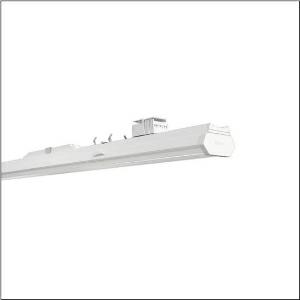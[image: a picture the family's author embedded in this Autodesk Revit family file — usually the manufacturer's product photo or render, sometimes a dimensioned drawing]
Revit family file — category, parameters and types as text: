
# Revit family: licross_r__21_protected_mo_52td1bdn4axg_daa2
name_source: partatom
category: Lighting Fixtures
units: mm (PartAtom-declared; Revit-internal decimal feet)

## family parameters
Cut with Voids When Loaded = No
Host = Face
Light Source = No
Part Type = Normal
Room Calculation Point = No
Round Connector Dimension = Use Diameter
Shared = No

## types (1)
- --- (1 x LED, 10050 lm, 62 W, 4000K)
    Apparent Load = 62 VA
    CIE Flux Codes = 54 82 95 97 100
    Color Rendering = 80
    Color Temperature = 4000K
    Default Elevation = 1800 mm
    Description = Licross® 21 Protected MO, luminaire insert, of sheet steel, galvanised, coil coated, white, length: 1.500mm, width: 90mm, height: 103mm, LED rated luminous flux: 10.060lm, light colour: 840, control gear: DALI 2, with plug, 5-pole, with phase selection, mains connection: 220..240V, AC, 50/60Hz, rated input power: 62W, halogen-free wiring, primary optical cover: cover, of PMMA, light emission: direct distribution, primary light characteristic: symmetric, protection rating (complete): IP54, insulation class (complete): insulation class I (protective earthing), certification: CE, ENEC, VDE, UKCA, protection symbol: D if used in an environment with non-conductive dust loads with corresponding accessories, impact resistance: IK06, permissible ambient temperature for indoor applications: -25..+35°C, corresponds to IFS (International Featured Standards) requirements for safety and quality in the food industry, reducing of maximum allowable ambient temperature of 5°C with ceiling mounting, LABS conformity tested according to VDMA 24364:2018-05, packaging unit: 1 piece
    Height = 92 mm
    Lamp = 1 x LED
    Lamp Light Flux = 10050 lm
    Lamp Power = 62 W
    Lamp count = 1
    Length = 1500 mm
    Luminous efficacy = 162 lm/W
    Manufacturer = Siteco
    ModVariant = No
    Model = 52TD1BDN4AXG
    Mounting Place = Ceiling
    Mounting Type = Pendant
    Number of Poles = 1
    OnlyDefault = Yes
    Power Factor = 1
    Product Name = Licross® 21 Protected MO
    Product group = luminaire insert
    ProductGroupID = 902
    Protection Class = Protection class I
    Protection Degree = IP 54
    RLX_Detail_Level = 1
    RLX_Emergency_Light_Flux = 0 lm
    RLX_Emergency_Type = 0
    RLX_Emergency_Type_DB = No
    RlxData = <blob elided: 24273 chars, md5=b6f0552b>
    Socket = socket
    Standby Power = 0 W
    System Light Flux = 10050 lm
    System Power = 62 W
    Type Comments = factory setting: luminous flux: 100 % | dim-lin: 254 | 418 mA
    Type Image = l_1256148.jpg
    URL = http://relux.com
    VarID = @adj_129054
    Voltage = 0 V
    Weight = 0.00 kg
    Width = 88 mm

## geometry (parser evidence)
native form markers: Blend x4, Sweep x11
no freeform markers — native parametric forms only
